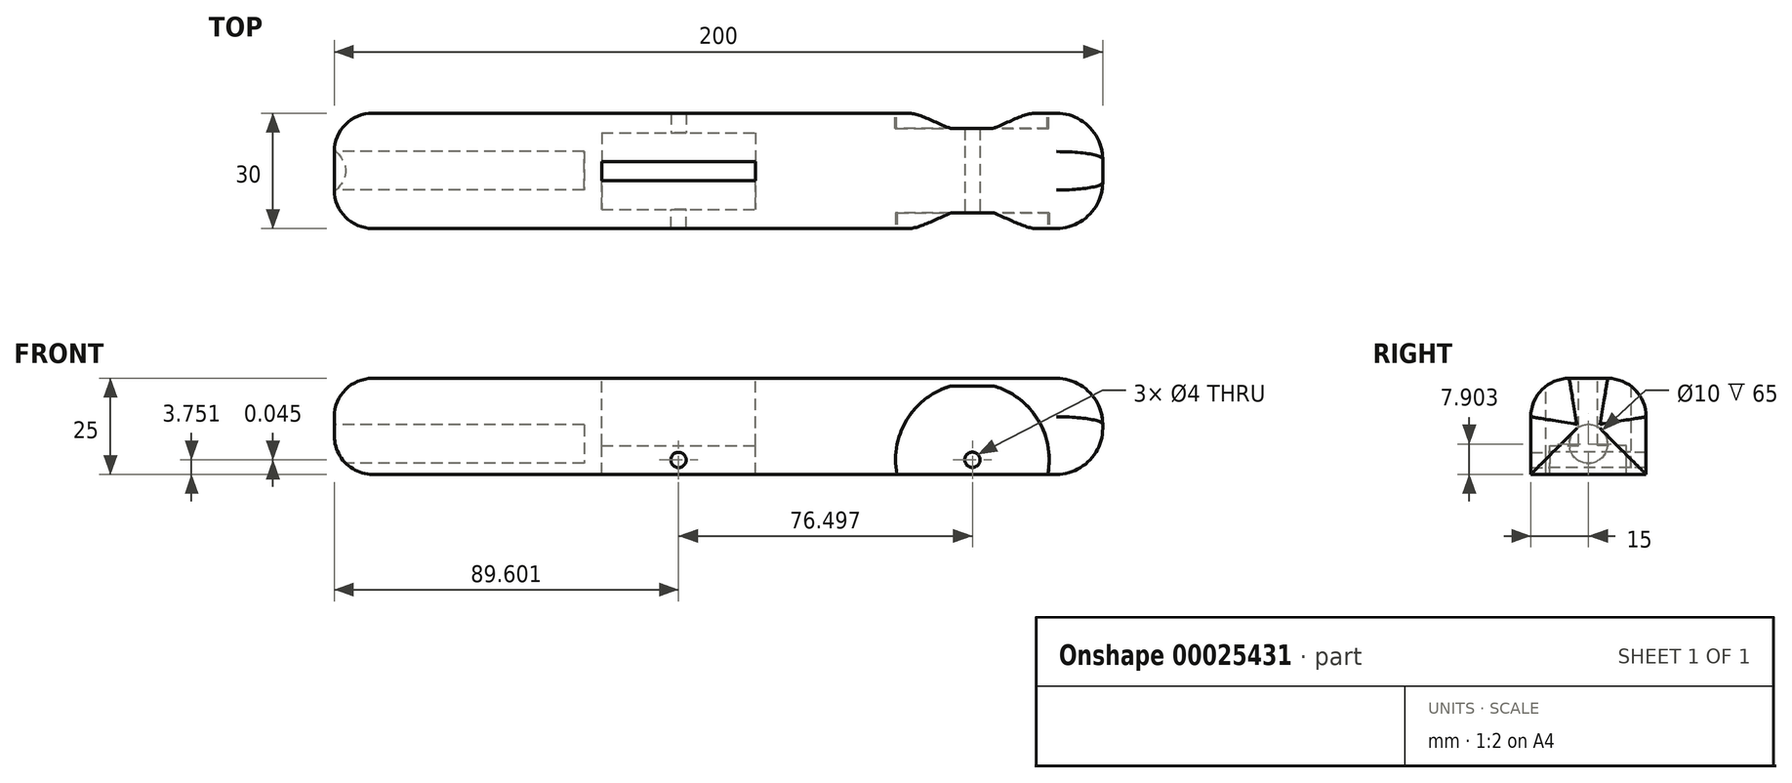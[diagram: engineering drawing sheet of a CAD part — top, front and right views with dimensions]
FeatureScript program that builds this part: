
annotation { "Feature Type Name" : "Feature", "Feature Type Description" : "" }
export const myFeature = defineFeature(function(context is Context, id is Id, definition is map)
    precondition{}
    {
        {
            var Q0;
            Q0=qCreatedBy(makeId("Front.planeOp"),FACE);
            var sketch = newSketch(context, id + "F0", { "sketchPlane" : qUnion([Q0])});
            skLineSegment(sketch, "E0.bottom", {"start": v(-84.2, -32.3) * mm, "end": v(115.8, -32.3) * mm});
            skLineSegment(sketch, "E0.top", {"start": v(-84.2, -7.3) * mm, "end": v(115.8, -7.3) * mm});
            skLineSegment(sketch, "E0.left", {"start": v(-84.2, -32.3) * mm, "end": v(-84.2, -7.3) * mm});
            skLineSegment(sketch, "E0.right", {"start": v(115.8, -32.3) * mm, "end": v(115.8, -7.3) * mm});
            skSolve(sketch);
        }
        {
            var Q0;
            Q0=makeQuery(id+"F0.imprint","IMPRINT",FACE,{"disambiguationData":[TD([[makeQuery(id+"F0.imprint","IMPRINT",EDGE,{"derivedFrom":sQuery(id+"F0.wireOp",EDGE,"E0.bottom")}),1.0]])]});
            extrude(context, id + "F1", {"entities" : qUnion([Q0]), "depth" : 30 * mm});
        }
        {
            var Q0;
            Q0=makeQuery(id+"F1.opExtrude","SWEPT_FACE",FACE,{"disambiguationData":[OSD([sQuery(id+"F0.wireOp",EDGE,"E0.left")])]});
            var sketch = newSketch(context, id + "F2", { "sketchPlane" : qUnion([Q0])});
            skCircle(sketch, "E1", {"center": v(15, -24.4) * mm, "radius": 5 * mm});
            skSolve(sketch);
        }
        {
            var Q0;
            Q0=makeQuery(id+"F2.imprint","IMPRINT",FACE,{"disambiguationData":[TD([[makeQuery(id+"F2.imprint","IMPRINT",EDGE,{"derivedFrom":sQuery(id+"F2.wireOp",EDGE,"E1")}),1.0]])]});
            extrude(context, id + "F3", {"entities" : qUnion([Q0]), "operationType" : NewBodyOperationType.REMOVE, "oppositeDirection" : true, "depth" : 65 * mm});
        }
        {
            var Q0;
            Q0=makeQuery(id+"F1.opExtrude","CAP_FACE",FACE,{"disambiguationData":[OSD([sQuery(id+"F0.wireOp",EDGE,"E0.bottom"),sQuery(id+"F0.wireOp",EDGE,"E0.top"),sQuery(id+"F0.wireOp",EDGE,"E0.left"),sQuery(id+"F0.wireOp",EDGE,"E0.right")])],"isStart":false});
            var sketch = newSketch(context, id + "F4", { "sketchPlane" : qUnion([Q0])});
            skCircle(sketch, "E2", {"center": v(81.9, -28.5) * mm, "radius": 2 * mm});
            skCircle(sketch, "E3", {"center": v(81.9, -28.5) * mm, "radius": 20 * mm});
            skSolve(sketch);
        }
        {
            var Q0;
            Q0=makeQuery(id+"F4.imprint","IMPRINT",FACE,{"disambiguationData":[TD([[makeQuery(id+"F4.imprint","IMPRINT",EDGE,{"derivedFrom":sQuery(id+"F4.wireOp",EDGE,"E2")}),1.0]])]});
            extrude(context, id + "F5", {"entities" : qUnion([Q0]), "operationType" : NewBodyOperationType.REMOVE, "endBound" : BoundingType.THROUGH_ALL, "oppositeDirection" : true, "depth" : 25 * mm});
        }
        {
            var Q0;
            Q0=makeQuery(id+"F0.imprint","IMPRINT",FACE,{"disambiguationData":[TD([[makeQuery(id+"F0.imprint","IMPRINT",EDGE,{"derivedFrom":sQuery(id+"F0.wireOp",EDGE,"E0.bottom")}),1.0]])]});
            var sketch = newSketch(context, id + "F6", { "sketchPlane" : qUnion([Q0])});
            skCircle(sketch, "E4", {"center": v(81.72, -28.53) * mm, "radius": 20 * mm});
            skSolve(sketch);
        }
        {
            var Q0;
            Q0 = qSketchRegion(id + "F6", true);
            extrude(context, id + "F7", {"entities" : qUnion([Q0]), "operationType" : NewBodyOperationType.REMOVE, "depth" : 4 * mm});
        }
        {
            var Q0;
            Q0=makeQuery(id+"F4.imprint","IMPRINT",FACE,{"disambiguationData":[TD([[makeQuery(id+"F4.imprint","IMPRINT",EDGE,{"derivedFrom":sQuery(id+"F4.wireOp",EDGE,"E2")}),-1.0]])]});
            extrude(context, id + "F8", {"entities" : qUnion([Q0]), "operationType" : NewBodyOperationType.REMOVE, "oppositeDirection" : true, "depth" : 4 * mm});
        }
        {
            var Q0;
            Q0=makeQuery(id+"F1.opExtrude","SWEPT_FACE",FACE,{"disambiguationData":[OSD([sQuery(id+"F0.wireOp",EDGE,"E0.top")])]});
            var sketch = newSketch(context, id + "F9", { "sketchPlane" : qUnion([Q0])});
            skLineSegment(sketch, "E5.bottom", {"start": v(-14.6, -12.56) * mm, "end": v(25.4, -12.56) * mm});
            skLineSegment(sketch, "E5.top", {"start": v(-14.6, -17.56) * mm, "end": v(25.4, -17.56) * mm});
            skLineSegment(sketch, "E5.left", {"start": v(-14.6, -12.56) * mm, "end": v(-14.6, -17.56) * mm});
            skLineSegment(sketch, "E5.right", {"start": v(25.4, -12.56) * mm, "end": v(25.4, -17.56) * mm});
            skSolve(sketch);
        }
        {
            var Q0;
            Q0=makeQuery(id+"F9.imprint","IMPRINT",FACE,{"disambiguationData":[TD([[makeQuery(id+"F9.imprint","IMPRINT",EDGE,{"derivedFrom":sQuery(id+"F9.wireOp",EDGE,"E5.bottom")}),-1.0]])]});
            extrude(context, id + "F10", {"entities" : qUnion([Q0]), "operationType" : NewBodyOperationType.REMOVE, "oppositeDirection" : true, "depth" : 30 * mm});
        }
        {
            var Q0;
            Q0=makeQuery(id+"F10.boolean.opBoolean","COPY",FACE,{"derivedFrom":makeQuery(id+"F10.opExtrude","SWEPT_FACE",FACE,{"disambiguationData":[OSD([sQuery(id+"F9.wireOp",EDGE,"E5.bottom")])]})});
            var sketch = newSketch(context, id + "F11", { "sketchPlane" : qUnion([Q0])});
            skLineSegment(sketch, "E6", {"start": v(-14.6, -32.3) * mm, "end": v(-14.6, -24.8) * mm});
            skLineSegment(sketch, "E7", {"start": v(-14.6, -24.8) * mm, "end": v(25.4, -24.8) * mm});
            skSolve(sketch);
        }
        {
            var Q0;
            Q0=makeQuery(id+"F11.imprint","IMPRINT",FACE,{"disambiguationData":[TD([[makeQuery(id+"F11.imprint","IMPRINT",EDGE,{"derivedFrom":sQuery(id+"F11.wireOp",EDGE,"9e564edc-9573-48ce-b113-e71f53215f2e")}),-1.0]])]});
            var Q1;
            Q1=makeQuery(id+"F11.imprint","IMPRINT",FACE,{"disambiguationData":[TD([[makeQuery(id+"F11.imprint","IMPRINT",EDGE,{"derivedFrom":sQuery(id+"F11.wireOp",EDGE,"E6")}),-1.0]])]});
            extrude(context, id + "F12", {"entities" : qUnion([Q0, Q1]), "operationType" : NewBodyOperationType.REMOVE, "oppositeDirection" : true, "depth" : 7.5 * mm});
        }
        {
            var Q0;
            Q0=makeQuery(id+"F12.boolean.opBoolean","COPY",FACE,{"derivedFrom":makeQuery(id+"F12.opExtrude","CAP_FACE",FACE,{"disambiguationData":[OSD([sQuery(id+"F9.wireOp",EDGE,"E5.bottom"),sQuery(id+"F9.wireOp",EDGE,"E5.right"),sQuery(id+"F11.wireOp",EDGE,"E6"),sQuery(id+"F11.wireOp",EDGE,"E7")])],"isStart":false})});
            var sketch = newSketch(context, id + "F13", { "sketchPlane" : qUnion([Q0])});
            skCircle(sketch, "E8", {"center": v(5.4, -28.55) * mm, "radius": 2 * mm});
            skSolve(sketch);
        }
        {
            var Q0;
            Q0=makeQuery(id+"F13.imprint","IMPRINT",FACE,{"disambiguationData":[TD([[makeQuery(id+"F13.imprint","IMPRINT",EDGE,{"derivedFrom":sQuery(id+"F13.wireOp",EDGE,"E8")}),1.0]])]});
            extrude(context, id + "F14", {"entities" : qUnion([Q0]), "operationType" : NewBodyOperationType.REMOVE, "oppositeDirection" : true, "depth" : 25 * mm});
        }
        {
            var Q0;
            Q0=makeQuery(id+"F10.boolean.opBoolean","COPY",FACE,{"derivedFrom":makeQuery(id+"F10.opExtrude","SWEPT_FACE",FACE,{"disambiguationData":[OSD([sQuery(id+"F9.wireOp",EDGE,"E5.top")])]})});
            var sketch = newSketch(context, id + "F15", { "sketchPlane" : qUnion([Q0])});
            skLineSegment(sketch, "E9", {"start": v(-25.4, -32.3) * mm, "end": v(-25.4, -24.8) * mm});
            skLineSegment(sketch, "E10", {"start": v(-25.4, -24.8) * mm, "end": v(14.6, -24.8) * mm});
            skSolve(sketch);
        }
        {
            var Q0;
            Q0=makeQuery(id+"F15.imprint","IMPRINT",FACE,{"disambiguationData":[TD([[makeQuery(id+"F15.imprint","IMPRINT",EDGE,{"derivedFrom":sQuery(id+"F15.wireOp",EDGE,"E9")}),-1.0]])]});
            extrude(context, id + "F16", {"entities" : qUnion([Q0]), "operationType" : NewBodyOperationType.REMOVE, "oppositeDirection" : true, "depth" : 7.5 * mm});
        }
        {
            var Q0;
            Q0=makeQuery(id+"F16.boolean.opBoolean","COPY",FACE,{"derivedFrom":makeQuery(id+"F16.opExtrude","CAP_FACE",FACE,{"disambiguationData":[OSD([sQuery(id+"F9.wireOp",EDGE,"E5.top"),sQuery(id+"F9.wireOp",EDGE,"E5.left"),sQuery(id+"F15.wireOp",EDGE,"E9"),sQuery(id+"F15.wireOp",EDGE,"E10")])],"isStart":false})});
            var sketch = newSketch(context, id + "F17", { "sketchPlane" : qUnion([Q0])});
            skCircle(sketch, "E11", {"center": v(-5.4, -28.55) * mm, "radius": 2 * mm});
            skSolve(sketch);
        }
        {
            var Q0;
            Q0=makeQuery(id+"F17.imprint","IMPRINT",FACE,{"disambiguationData":[TD([[makeQuery(id+"F17.imprint","IMPRINT",EDGE,{"derivedFrom":sQuery(id+"F17.wireOp",EDGE,"E11")}),1.0]])]});
            extrude(context, id + "F18", {"entities" : qUnion([Q0]), "operationType" : NewBodyOperationType.REMOVE, "oppositeDirection" : true, "depth" : 25 * mm});
        }
        {
            var Q0;
            Q0=makeQuery(id+"F1.opExtrude","CAP_EDGE",EDGE,{"disambiguationData":[OSD([sQuery(id+"F0.wireOp",EDGE,"E0.top")])],"isStart":false});
            var Q1;
            Q1=makeQuery(id+"F1.opExtrude","CAP_EDGE",EDGE,{"disambiguationData":[OSD([sQuery(id+"F0.wireOp",EDGE,"E0.top")])],"isStart":true});
            var Q2;
            Q2=makeQuery(id+"F1.opExtrude","CAP_EDGE",EDGE,{"disambiguationData":[OSD([sQuery(id+"F0.wireOp",EDGE,"E0.left")])],"isStart":false});
            var Q3;
            Q3=makeQuery(id+"F1.opExtrude","SWEPT_EDGE",EDGE,{"disambiguationData":[OSD([sQuery(id+"F0.wireOp",EDGE,"E0.bottom"),sQuery(id+"F0.wireOp",EDGE,"E0.left")])]});
            var Q4;
            Q4=makeQuery(id+"F1.opExtrude","SWEPT_EDGE",EDGE,{"disambiguationData":[OSD([sQuery(id+"F0.wireOp",EDGE,"E0.top"),sQuery(id+"F0.wireOp",EDGE,"E0.left")])]});
            var Q5;
            Q5=makeQuery(id+"F1.opExtrude","CAP_EDGE",EDGE,{"disambiguationData":[OSD([sQuery(id+"F0.wireOp",EDGE,"E0.left")])],"isStart":true});
            fillet(context, id + "F19", {"entities" : qUnion([Q0, Q1, Q2, Q3, Q4, Q5]), "radius" : 10 * mm, "tangentPropagation" : true, "allowEdgeOverflow" : false});
        }
        {
            var Q0;
            Q0=makeQuery(id+"F1.opExtrude","SWEPT_EDGE",EDGE,{"disambiguationData":[OSD([sQuery(id+"F0.wireOp",EDGE,"E0.bottom"),sQuery(id+"F0.wireOp",EDGE,"E0.right")])]});
            var Q1;
            Q1=makeQuery(id+"F1.opExtrude","SWEPT_FACE",FACE,{"disambiguationData":[OSD([sQuery(id+"F0.wireOp",EDGE,"E0.right")])]});
            var Q2;
            Q2=makeQuery(id+"F1.opExtrude","SWEPT_EDGE",EDGE,{"disambiguationData":[OSD([sQuery(id+"F0.wireOp",EDGE,"E0.top"),sQuery(id+"F0.wireOp",EDGE,"E0.right")])]});
            fillet(context, id + "F20", {"entities" : qUnion([Q0, Q1, Q2]), "radius" : 12 * mm, "tangentPropagation" : true, "allowEdgeOverflow" : false});
        }
    });
